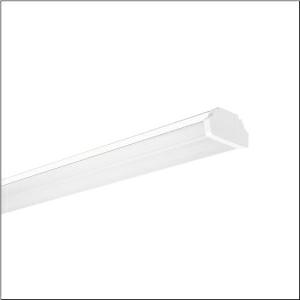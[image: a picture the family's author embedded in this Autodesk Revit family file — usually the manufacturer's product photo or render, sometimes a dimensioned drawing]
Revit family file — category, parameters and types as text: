
# Revit family: dus_31_gen_2_53bd812mv4a5c2_35bc
name_source: partatom
category: Lighting Fixtures
units: mm (PartAtom-declared; Revit-internal decimal feet)

## family parameters
Cut with Voids When Loaded = No
Host = Face
Light Source = No
Part Type = Normal
Room Calculation Point = No
Round Connector Dimension = Use Diameter
Shared = No

## types (1)
- --- (1 x LED, 10960 lm, 60.5 W, 4000K)
    Apparent Load = 61 VA
    CIE Flux Codes = 47 80 95 93 100
    Color Rendering = 80
    Color Temperature = 4000K
    Default Elevation = 1800 mm
    Description = DUS 31 Gen.2, luminaire insert, of sheet steel, coil coated, white, length: 1.535mm, width: 81mm, height: 90mm, 5x system unit, system units: 307mm, LED rated luminous flux: 10.960lm, light colour: 840, SDCM (Standard Deviation of Colour Matching)MacAdam ≤ 3 SDCM (initial), control gear: ON/OFF Multilumen, control gear: ECG, with plug, 3-pole, with phase selection, mains connection: 220..240V, AC, 50/60Hz, rated input power: 61W, through-wiring accessed according to module size, primary optical cover: cover, of PMMA, light emission: direct distribution, primary light characteristic: symmetric, protection rating (complete): IP20, protection rating (LED compartment): IP50, insulation class (complete): insulation class I (protective earthing), certification: CE, ENEC, VDE, UKCA, impact resistance: IK03, permissible ambient temperature for indoor applications: -35..+40°C, corresponds to IFS (International Featured Standards) requirements for safety and quality in the food industry, reducing of maximum allowable ambient temperature of 5°C with ceiling mounting, packaging unit: 1 piece
    Height = 95 mm
    Lamp = 1 x LED
    Lamp Light Flux = 10960 lm
    Lamp Power = 60.5 W
    Lamp count = 1
    Length = 1535 mm
    Luminous efficacy = 181 lm/W
    Manufacturer = Siteco
    ModVariant = No
    Model = 53BD812MV4A5C2
    Mounting Place = Ceiling
    Mounting Type = Pendant
    Number of Poles = 1
    OnlyDefault = Yes
    Power Factor = 1
    Product Name = DUS 31 Gen.2
    Product group = luminaire insert | ceiling pendant
    ProductGroupID = 901
    Protection Class = Protection class I
    Protection Degree = IP 20
    RLX_Detail_Level = 1
    RLX_Emergency_Light_Flux = 0 lm
    RLX_Emergency_Type = 0
    RLX_Emergency_Type_DB = No
    RlxData = <blob elided: 29889 chars, md5=2a9c0b08>
    Socket = socket
    Standby Power = 0 W
    System Light Flux = 10960 lm
    System Power = 61 W
    Type Comments = factory setting: luminous flux: 100 % | (A | C | E) | 140 mA
    Type Image = l_1319596.jpg
    URL = http://relux.com
    VarID = @adj_051287
    Voltage = 0 V
    Weight = 0.00 kg
    Width = 81 mm

## geometry (parser evidence)
native form markers: Blend x4, Sweep x13
no freeform markers — native parametric forms only
